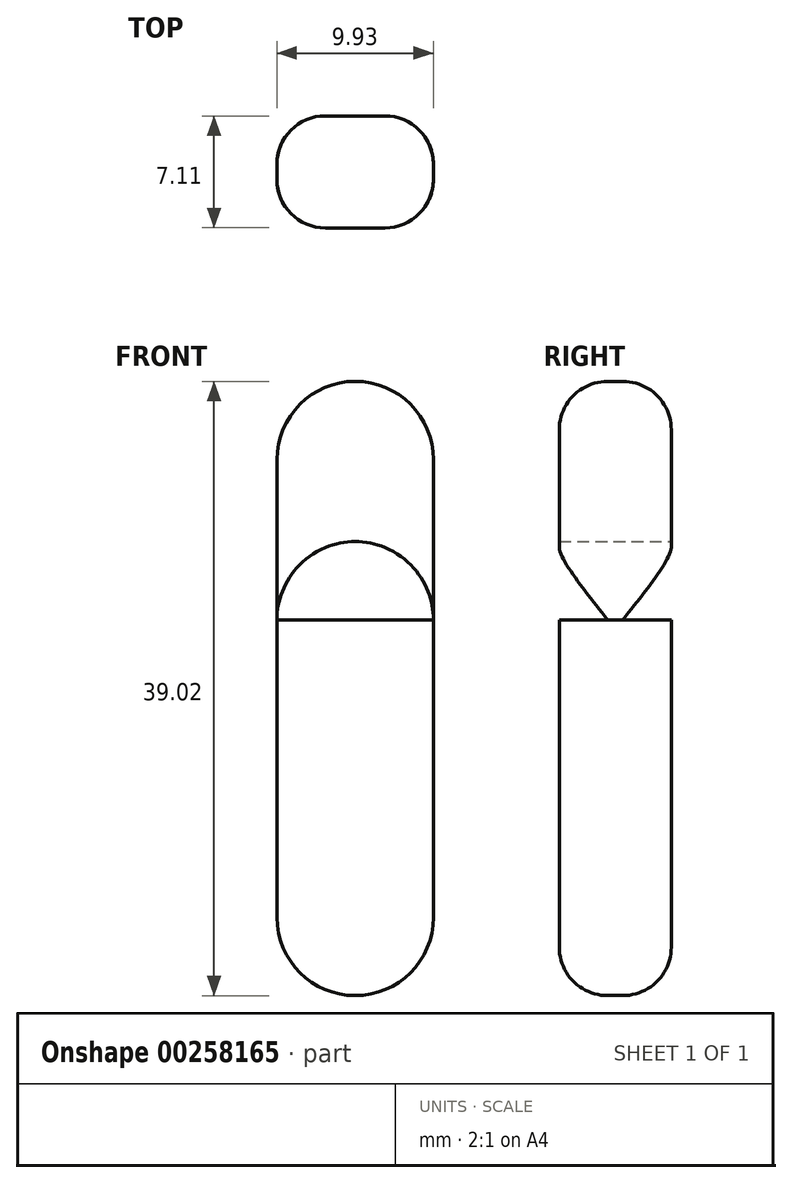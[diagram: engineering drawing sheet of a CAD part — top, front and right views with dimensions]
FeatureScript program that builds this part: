
annotation { "Feature Type Name" : "Feature", "Feature Type Description" : "" }
export const myFeature = defineFeature(function(context is Context, id is Id, definition is map)
    precondition{}
    {
        {
            var Q0;
            Q0=qCreatedBy(makeId("Front.planeOp"),FACE);
            var sketch = newSketch(context, id + "F0", { "sketchPlane" : qUnion([Q0])});
            skLineSegment(sketch, "E0", {"start": v(5.31, -23.5) * mm, "end": v(5.31, -4.6) * mm});
            skLineSegment(sketch, "E1", {"start": v(-4.62, -23.5) * mm, "end": v(-4.62, -4.6) * mm});
            skLineSegment(sketch, "E2", {"start": v(-4.62, -4.6) * mm, "end": v(-4.62, 2.38) * mm});
            skArc(sketch, "E3", {"start": v(-4.62, -4.6) * mm, "mid": v(0.35, 0.37) * mm, "end": v(5.31, -4.6) * mm});
            skArc(sketch, "E4", {"start": v(-4.62, -4.6) * mm, "mid": v(0.35, -9.57) * mm, "end": v(5.31, -4.6) * mm});
            skLineSegment(sketch, "E5", {"start": v(-4.62, -4.6) * mm, "end": v(5.31, -4.6) * mm});
            skLineSegment(sketch, "E6", {"start": v(5.31, -4.6) * mm, "end": v(5.31, 5.58) * mm});
            skLineSegment(sketch, "E7", {"start": v(-4.62, 2.38) * mm, "end": v(-4.62, 5.58) * mm});
            skArc(sketch, "E8", {"start": v(-4.62, 5.58) * mm, "mid": v(0.35, 10.55) * mm, "end": v(5.31, 5.58) * mm});
            skArc(sketch, "E9", {"start": v(-4.62, -23.5) * mm, "mid": v(0.35, -28.47) * mm, "end": v(5.31, -23.5) * mm});
            skSolve(sketch);
        }
        {
            var Q0;
            Q0=makeQuery(id+"F0.imprint","IMPRINT",FACE,{"disambiguationData":[TD([[makeQuery(id+"F0.imprint","IMPRINT",EDGE,{"derivedFrom":sQuery(id+"F0.wireOp",EDGE,"E2")}),-1.0]])]});
            var Q1;
            Q1=makeQuery(id+"F0.imprint","IMPRINT",FACE,{"disambiguationData":[TD([[makeQuery(id+"F0.imprint","IMPRINT",EDGE,{"derivedFrom":sQuery(id+"F0.wireOp",EDGE,"E4")}),1.0]])]});
            var Q2;
            Q2=makeQuery(id+"F0.imprint","IMPRINT",FACE,{"disambiguationData":[TD([[makeQuery(id+"F0.imprint","IMPRINT",EDGE,{"derivedFrom":sQuery(id+"F0.wireOp",EDGE,"E3")}),-1.0]])]});
            var Q3;
            Q3=makeQuery(id+"F0.imprint","IMPRINT",FACE,{"disambiguationData":[TD([[makeQuery(id+"F0.imprint","IMPRINT",EDGE,{"derivedFrom":sQuery(id+"F0.wireOp",EDGE,"E0")}),1.0]])]});
            extrude(context, id + "F1", {"entities" : qUnion([Q0, Q1, Q2, Q3]), "depth" : 7.11 * mm});
        }
        {
            var Q0;
            Q0=makeQuery(id+"F1.opExtrude","CAP_EDGE",EDGE,{"disambiguationData":[OSD([sQuery(id+"F0.wireOp",EDGE,"E0"),sQuery(id+"F0.wireOp",EDGE,"E6")])],"isStart":false});
            var Q1;
            Q1=makeQuery(id+"F1.opExtrude","CAP_EDGE",EDGE,{"disambiguationData":[OSD([sQuery(id+"F0.wireOp",EDGE,"E0"),sQuery(id+"F0.wireOp",EDGE,"E6")])],"isStart":true});
            var Q2;
            Q2=makeQuery(id+"F1.opExtrude","CAP_EDGE",EDGE,{"disambiguationData":[OSD([sQuery(id+"F0.wireOp",EDGE,"E8")])],"isStart":false});
            var Q3;
            Q3=makeQuery(id+"F1.opExtrude","CAP_EDGE",EDGE,{"disambiguationData":[OSD([sQuery(id+"F0.wireOp",EDGE,"E8")])],"isStart":true});
            var Q4;
            Q4=makeQuery(id+"F1.opExtrude","CAP_EDGE",EDGE,{"disambiguationData":[OSD([sQuery(id+"F0.wireOp",EDGE,"E9")])],"isStart":false});
            var Q5;
            Q5=makeQuery(id+"F1.opExtrude","CAP_EDGE",EDGE,{"disambiguationData":[OSD([sQuery(id+"F0.wireOp",EDGE,"E1"),sQuery(id+"F0.wireOp",EDGE,"E2"),sQuery(id+"F0.wireOp",EDGE,"E7")])],"isStart":true});
            var Q6;
            Q6=makeQuery(id+"F1.opExtrude","CAP_EDGE",EDGE,{"disambiguationData":[OSD([sQuery(id+"F0.wireOp",EDGE,"E1"),sQuery(id+"F0.wireOp",EDGE,"E2"),sQuery(id+"F0.wireOp",EDGE,"E7")])],"isStart":false});
            fillet(context, id + "F2", {"entities" : qUnion([Q0, Q1, Q2, Q3, Q4, Q5, Q6]), "radius" : 3.07 * mm, "tangentPropagation" : true, "allowEdgeOverflow" : false});
        }
    });
